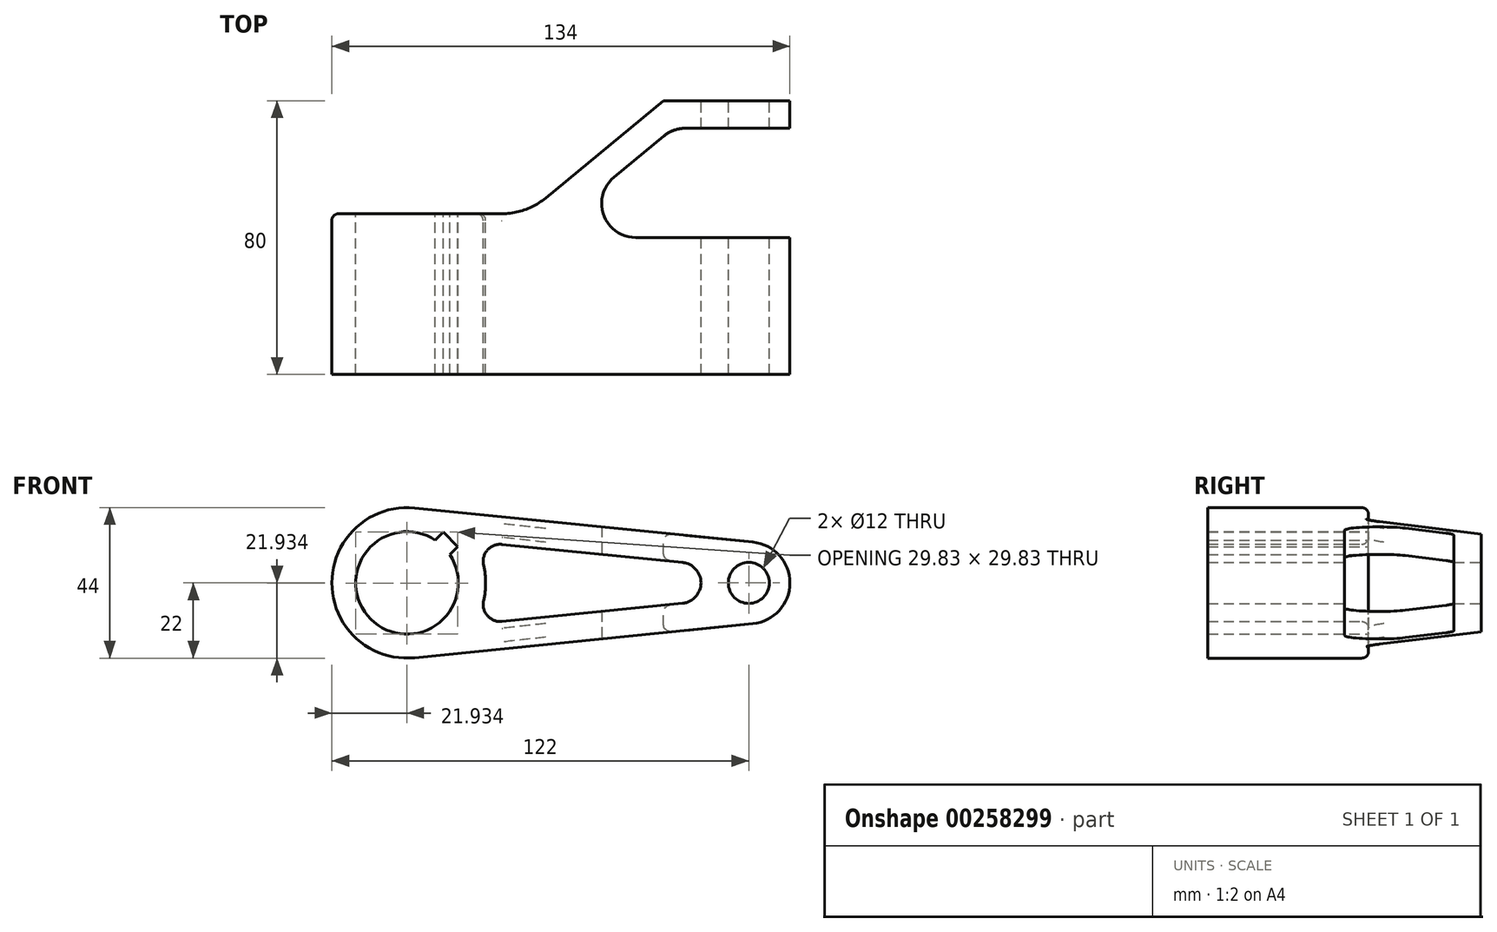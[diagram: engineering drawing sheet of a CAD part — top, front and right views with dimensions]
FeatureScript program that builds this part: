
annotation { "Feature Type Name" : "Feature", "Feature Type Description" : "" }
export const myFeature = defineFeature(function(context is Context, id is Id, definition is map)
    precondition{}
    {
        {
            var Q0;
            Q0=qCreatedBy(makeId("Front.planeOp"),FACE);
            var sketch = newSketch(context, id + "F0", { "sketchPlane" : qUnion([Q0])});
            skArc(sketch, "E0", {"start": v(2.2, 21.89) * mm, "mid": v(-22, 0) * mm, "end": v(2.2, -21.89) * mm});
            skLineSegment(sketch, "E1", {"start": v(2.2, 21.89) * mm, "end": v(101.2, 11.94) * mm});
            skLineSegment(sketch, "E2", {"start": v(2.2, -21.89) * mm, "end": v(101.2, -11.94) * mm});
            skArc(sketch, "E3", {"start": v(101.2, -11.94) * mm, "mid": v(112, 0) * mm, "end": v(101.2, 11.94) * mm});
            skArc(sketch, "E4", {"start": v(8.27, 12.51) * mm, "mid": v(-10.6, -10.6) * mm, "end": v(12.51, 8.27) * mm});
            skCircle(sketch, "E5", {"center": v(100, 0) * mm, "radius": 6 * mm});
            skLineSegment(sketch, "E6", {"start": v(0, 0) * mm, "end": v(100, 0) * mm, "construction": true});
            skArc(sketch, "E7", {"start": v(22.4, -5.18) * mm, "mid": v(23, 0) * mm, "end": v(22.4, 5.18) * mm});
            skLineSegment(sketch, "E8.0", {"start": v(27.78, 11.28) * mm, "end": v(80.6, 5.97) * mm});
            skLineSegment(sketch, "E9.0", {"start": v(27.78, -11.28) * mm, "end": v(80.6, -5.97) * mm});
            skArc(sketch, "E10", {"start": v(80.6, -5.97) * mm, "mid": v(86, 0) * mm, "end": v(80.6, 5.97) * mm});
            skPoint(sketch, "E11.visualSharp", {"position": v(19.56, 12.1) * mm});
            skArc(sketch, "E11.filletArc", {"start": v(27.78, 11.28) * mm, "mid": v(23.53, 9.6) * mm, "end": v(22.4, 5.18) * mm});
            skPoint(sketch, "E12.visualSharp", {"position": v(19.56, -12.1) * mm});
            skArc(sketch, "E12.filletArc", {"start": v(22.4, -5.18) * mm, "mid": v(23.53, -9.6) * mm, "end": v(27.78, -11.28) * mm});
            skLineSegment(sketch, "E13", {"start": v(8.27, 12.51) * mm, "end": v(10.6, 14.85) * mm});
            skLineSegment(sketch, "E14", {"start": v(10.6, 14.85) * mm, "end": v(14.85, 10.6) * mm});
            skLineSegment(sketch, "E15", {"start": v(14.85, 10.6) * mm, "end": v(12.51, 8.27) * mm});
            skLineSegment(sketch, "E16", {"start": v(0, 0) * mm, "end": v(12.73, 12.73) * mm, "construction": true});
            skArc(sketch, "E17", {"start": v(12.51, 8.27) * mm, "mid": v(10.6, 10.6) * mm, "end": v(8.27, 12.51) * mm});
            skSolve(sketch);
        }
        {
            var Q0;
            Q0 = qSketchRegion(id + "F0", true);
            extrude(context, id + "F1", {"entities" : qUnion([Q0]), "endBound" : BoundingType.SYMMETRIC, "offsetDistance" : 25 * mm, "depth" : 80 * mm});
        }
        {
            var Q0;
            Q0=qCreatedBy(makeId("Top.planeOp"),FACE);
            var sketch = newSketch(context, id + "F2", { "sketchPlane" : qUnion([Q0])});
            skLineSegment(sketch, "E18", {"start": v(-22, 7) * mm, "end": v(-22, 40) * mm});
            skLineSegment(sketch, "E19", {"start": v(112, 32) * mm, "end": v(112, 0) * mm});
            skLineSegment(sketch, "E20", {"start": v(-22, 40) * mm, "end": v(75, 40) * mm});
            skLineSegment(sketch, "E21", {"start": v(75, 40) * mm, "end": v(35, 7) * mm});
            skLineSegment(sketch, "E22", {"start": v(35, 7) * mm, "end": v(-22, 7) * mm});
            skLineSegment(sketch, "E23", {"start": v(-22, 0) * mm, "end": v(112, 0) * mm, "construction": true});
            skLineSegment(sketch, "E24", {"start": v(0, 40) * mm, "end": v(0, -40) * mm, "construction": true});
            skLineSegment(sketch, "E25", {"start": v(112, 32) * mm, "end": v(77.87, 32) * mm});
            skLineSegment(sketch, "E26", {"start": v(77.87, 32) * mm, "end": v(39.09, 0) * mm});
            skLineSegment(sketch, "E27", {"start": v(39.09, 0) * mm, "end": v(112, 0) * mm});
            skPoint(sketch, "E28.orphan", {"position": v(112, 40) * mm});
            skPoint(sketch, "E29.orphan", {"position": v(112, -40) * mm});
            skPoint(sketch, "E30.orphan", {"position": v(-22, -40) * mm});
            skSolve(sketch);
        }
        {
            var Q0;
            Q0 = qSketchRegion(id + "F2", true);
            extrude(context, id + "F3", {"entities" : qUnion([Q0]), "operationType" : NewBodyOperationType.REMOVE, "endBound" : BoundingType.THROUGH_ALL, "oppositeDirection" : true, "depth" : 25 * mm, "hasSecondDirection" : true, "secondDirectionBound" : SecondDirectionBoundingType.THROUGH_ALL, "secondDirectionOppositeDirection" : false, "secondDirectionDepth" : 25 * mm});
        }
        {
            var Q0;
            {var subQ0=sQuery(id+"F2.wireOp",EDGE,"E27");var subQ1=sQuery(id+"F2.wireOp",EDGE,"E26");Q0=makeQuery(id+"Fcrfvm8RNoEdja2_1.1.F3.boolean.opBoolean","MERGE",EDGE,{"derivedFrom":[makeQuery(id+"F3.boolean.opBoolean","COPY",EDGE,{"disambiguationData":[TD([makeQuery(id+"F1.opExtrude","SWEPT_FACE",FACE,{"disambiguationData":[OSD([sQuery(id+"F0.wireOp",EDGE,"E1")])]})])],"derivedFrom":makeQuery(id+"F3.opExtrude","SWEPT_EDGE",EDGE,{"disambiguationData":[OSD([subQ1,subQ0])]})}),makeQuery(id+"Fcrfvm8RNoEdja2_1.1.F3.opExtrude","SWEPT_EDGE",EDGE,{"disambiguationData":[OSD([subQ1,subQ0])]})]});}
            var Q1;
            {var subQ0=sQuery(id+"F2.wireOp",EDGE,"E27");var subQ1=sQuery(id+"F2.wireOp",EDGE,"E26");Q1=makeQuery(id+"Fcrfvm8RNoEdja2_1.1.F3.boolean.opBoolean","MERGE",EDGE,{"derivedFrom":[makeQuery(id+"F3.boolean.opBoolean","COPY",EDGE,{"disambiguationData":[TD([makeQuery(id+"F1.opExtrude","SWEPT_FACE",FACE,{"disambiguationData":[OSD([sQuery(id+"F0.wireOp",EDGE,"E2")])]})])],"derivedFrom":makeQuery(id+"F3.opExtrude","SWEPT_EDGE",EDGE,{"disambiguationData":[OSD([subQ1,subQ0])]})}),makeQuery(id+"Fcrfvm8RNoEdja2_1.1.F3.opExtrude","SWEPT_EDGE",EDGE,{"disambiguationData":[OSD([subQ1,subQ0])]})]});}
            var Q2;
            {var subQ0=sQuery(id+"F2.wireOp",EDGE,"E25");var subQ1=sQuery(id+"F2.wireOp",EDGE,"E26");Q2=makeQuery(id+"F3.boolean.opBoolean","COPY",EDGE,{"disambiguationData":[TD([makeQuery(id+"F1.opExtrude","SWEPT_FACE",FACE,{"disambiguationData":[OSD([sQuery(id+"F0.wireOp",EDGE,"E1")])]})])],"derivedFrom":makeQuery(id+"F3.opExtrude","SWEPT_EDGE",EDGE,{"disambiguationData":[OSD([subQ0,subQ1])]})});}
            var Q3;
            {var subQ0=sQuery(id+"F2.wireOp",EDGE,"E25");var subQ1=sQuery(id+"F2.wireOp",EDGE,"E26");Q3=makeQuery(id+"F3.boolean.opBoolean","COPY",EDGE,{"disambiguationData":[TD([makeQuery(id+"F1.opExtrude","SWEPT_FACE",FACE,{"disambiguationData":[OSD([sQuery(id+"F0.wireOp",EDGE,"E2")])]})])],"derivedFrom":makeQuery(id+"F3.opExtrude","SWEPT_EDGE",EDGE,{"disambiguationData":[OSD([subQ0,subQ1])]})});}
            var Q4;
            {var subQ0=sQuery(id+"F2.wireOp",EDGE,"E25");var subQ1=sQuery(id+"F2.wireOp",EDGE,"E26");Q4=makeQuery(id+"Fcrfvm8RNoEdja2_1.1.F3.boolean.opBoolean","COPY",EDGE,{"disambiguationData":[TD([makeQuery(id+"F1.opExtrude","SWEPT_FACE",FACE,{"disambiguationData":[OSD([sQuery(id+"F0.wireOp",EDGE,"E2")])]})])],"derivedFrom":makeQuery(id+"Fcrfvm8RNoEdja2_1.1.F3.opExtrude","SWEPT_EDGE",EDGE,{"disambiguationData":[OSD([subQ0,subQ1])]})});}
            var Q5;
            {var subQ0=sQuery(id+"F2.wireOp",EDGE,"E26");var subQ1=sQuery(id+"F2.wireOp",EDGE,"E25");Q5=makeQuery(id+"Fcrfvm8RNoEdja2_1.1.F3.boolean.opBoolean","COPY",EDGE,{"disambiguationData":[TD([makeQuery(id+"F1.opExtrude","SWEPT_FACE",FACE,{"disambiguationData":[OSD([sQuery(id+"F0.wireOp",EDGE,"E1")])]})])],"derivedFrom":makeQuery(id+"Fcrfvm8RNoEdja2_1.1.F3.opExtrude","SWEPT_EDGE",EDGE,{"disambiguationData":[OSD([subQ1,subQ0])]})});}
            fillet(context, id + "F4", {"entities" : qUnion([Q0, Q1, Q2, Q3, Q4, Q5]), "radius" : 10 * mm, "tangentPropagation" : true, "allowEdgeOverflow" : false});
        }
        {
            var Q0;
            {var subQ1=sQuery(id+"F0.wireOp",EDGE,"E1");var subQ2=sQuery(id+"F2.wireOp",EDGE,"E21");Q0=makeQuery(id+"F3.boolean.opBoolean","COPY",EDGE,{"disambiguationData":[TD([makeQuery(id+"F1.opExtrude","SWEPT_FACE",FACE,{"disambiguationData":[OSD([subQ1])]})])],"derivedFrom":makeQuery(id+"F3.opExtrude","SWEPT_EDGE",EDGE,{"disambiguationData":[OSD([sQuery(id+"F2.wireOp",EDGE,"E20"),subQ2])]})});}
            var Q1;
            {var subQ1=sQuery(id+"F0.wireOp",EDGE,"E2");var subQ2=sQuery(id+"F2.wireOp",EDGE,"E21");Q1=makeQuery(id+"F3.boolean.opBoolean","COPY",EDGE,{"disambiguationData":[TD([makeQuery(id+"F1.opExtrude","SWEPT_FACE",FACE,{"disambiguationData":[OSD([subQ1])]})])],"derivedFrom":makeQuery(id+"F3.opExtrude","SWEPT_EDGE",EDGE,{"disambiguationData":[OSD([sQuery(id+"F2.wireOp",EDGE,"E20"),subQ2])]})});}
            var Q2;
            {var subQ0=sQuery(id+"F2.wireOp",EDGE,"E21");var subQ1=sQuery(id+"F2.wireOp",EDGE,"E22");Q2=makeQuery(id+"F3.boolean.opBoolean","COPY",EDGE,{"disambiguationData":[TD([makeQuery(id+"F1.opExtrude","SWEPT_FACE",FACE,{"disambiguationData":[OSD([sQuery(id+"F0.wireOp",EDGE,"E2")])]})])],"derivedFrom":makeQuery(id+"F3.opExtrude","SWEPT_EDGE",EDGE,{"disambiguationData":[OSD([subQ0,subQ1])]})});}
            var Q3;
            {var subQ0=sQuery(id+"F2.wireOp",EDGE,"E21");var subQ1=sQuery(id+"F2.wireOp",EDGE,"E22");Q3=makeQuery(id+"F3.boolean.opBoolean","COPY",EDGE,{"disambiguationData":[TD([makeQuery(id+"F1.opExtrude","SWEPT_FACE",FACE,{"disambiguationData":[OSD([sQuery(id+"F0.wireOp",EDGE,"E1")])]})])],"derivedFrom":makeQuery(id+"F3.opExtrude","SWEPT_EDGE",EDGE,{"disambiguationData":[OSD([subQ0,subQ1])]})});}
            var Q4;
            {var subQ0=sQuery(id+"F2.wireOp",EDGE,"E21");var subQ1=sQuery(id+"F2.wireOp",EDGE,"E22");Q4=makeQuery(id+"Fcrfvm8RNoEdja2_1.1.F3.boolean.opBoolean","COPY",EDGE,{"disambiguationData":[TD([makeQuery(id+"F1.opExtrude","SWEPT_FACE",FACE,{"disambiguationData":[OSD([sQuery(id+"F0.wireOp",EDGE,"E1")])]})])],"derivedFrom":makeQuery(id+"Fcrfvm8RNoEdja2_1.1.F3.opExtrude","SWEPT_EDGE",EDGE,{"disambiguationData":[OSD([subQ0,subQ1])]})});}
            var Q5;
            {var subQ0=sQuery(id+"F2.wireOp",EDGE,"E21");var subQ1=sQuery(id+"F2.wireOp",EDGE,"E22");Q5=makeQuery(id+"Fcrfvm8RNoEdja2_1.1.F3.boolean.opBoolean","COPY",EDGE,{"disambiguationData":[TD([makeQuery(id+"F1.opExtrude","SWEPT_FACE",FACE,{"disambiguationData":[OSD([sQuery(id+"F0.wireOp",EDGE,"E2")])]})])],"derivedFrom":makeQuery(id+"Fcrfvm8RNoEdja2_1.1.F3.opExtrude","SWEPT_EDGE",EDGE,{"disambiguationData":[OSD([subQ0,subQ1])]})});}
            var Q6;
            {var subQ1=sQuery(id+"F0.wireOp",EDGE,"E2");var subQ2=sQuery(id+"F2.wireOp",EDGE,"E21");Q6=makeQuery(id+"Fcrfvm8RNoEdja2_1.1.F3.boolean.opBoolean","COPY",EDGE,{"disambiguationData":[TD([makeQuery(id+"F1.opExtrude","SWEPT_FACE",FACE,{"disambiguationData":[OSD([subQ1])]})])],"derivedFrom":makeQuery(id+"Fcrfvm8RNoEdja2_1.1.F3.opExtrude","SWEPT_EDGE",EDGE,{"disambiguationData":[OSD([sQuery(id+"F2.wireOp",EDGE,"E20"),subQ2])]})});}
            var Q7;
            {var subQ1=sQuery(id+"F0.wireOp",EDGE,"E1");var subQ2=sQuery(id+"F2.wireOp",EDGE,"E21");Q7=makeQuery(id+"Fcrfvm8RNoEdja2_1.1.F3.boolean.opBoolean","COPY",EDGE,{"disambiguationData":[TD([makeQuery(id+"F1.opExtrude","SWEPT_FACE",FACE,{"disambiguationData":[OSD([subQ1])]})])],"derivedFrom":makeQuery(id+"Fcrfvm8RNoEdja2_1.1.F3.opExtrude","SWEPT_EDGE",EDGE,{"disambiguationData":[OSD([sQuery(id+"F2.wireOp",EDGE,"E20"),subQ2])]})});}
            fillet(context, id + "F5", {"entities" : qUnion([Q0, Q1, Q2, Q3, Q4, Q5, Q6, Q7]), "radius" : 20 * mm, "tangentPropagation" : true, "allowEdgeOverflow" : false});
        }
        {
            var Q0;
            Q0=makeQuery(id+"Fcrfvm8RNoEdja2_1.1.F3.boolean.opBoolean","INTERSECT",EDGE,{"derivedFrom":[makeQuery(id+"F1.opExtrude","SWEPT_FACE",FACE,{"disambiguationData":[OSD([sQuery(id+"F0.wireOp",EDGE,"E0")])]}),makeQuery(id+"Fcrfvm8RNoEdja2_1.1.F3.opExtrude","SWEPT_FACE",FACE,{"disambiguationData":[OSD([sQuery(id+"F2.wireOp",EDGE,"E22")])]})]});
            var Q1;
            Q1=makeQuery(id+"F3.boolean.opBoolean","INTERSECT",EDGE,{"derivedFrom":[makeQuery(id+"F1.opExtrude","SWEPT_FACE",FACE,{"disambiguationData":[OSD([sQuery(id+"F0.wireOp",EDGE,"E0")])]}),makeQuery(id+"F3.opExtrude","SWEPT_FACE",FACE,{"disambiguationData":[OSD([sQuery(id+"F2.wireOp",EDGE,"E22")])]})]});
            var Q2;
            {var subQ0=makeQuery(id+"F1.opExtrude","SWEPT_FACE",FACE,{"disambiguationData":[OSD([sQuery(id+"F0.wireOp",EDGE,"E8.0")])]});var subQ1=sQuery(id+"F2.wireOp",EDGE,"E22");var subQ2=sQuery(id+"F2.wireOp",EDGE,"E21");Q2=makeQuery(id+"F5.opFillet","BLEND_EDGE",EDGE,{"blendedFrom":[makeQuery(id+"Fcrfvm8RNoEdja2_1.1.F3.boolean.opBoolean","COPY",EDGE,{"disambiguationData":[TD([makeQuery(id+"F1.opExtrude","SWEPT_FACE",FACE,{"disambiguationData":[OSD([sQuery(id+"F0.wireOp",EDGE,"E1")])]})])],"derivedFrom":makeQuery(id+"Fcrfvm8RNoEdja2_1.1.F3.opExtrude","SWEPT_EDGE",EDGE,{"disambiguationData":[OSD([subQ2,subQ1])]})}),subQ0],"blendedInto":[subQ0]});}
            var Q3;
            {var subQ0=makeQuery(id+"F1.opExtrude","SWEPT_FACE",FACE,{"disambiguationData":[OSD([sQuery(id+"F0.wireOp",EDGE,"E8.0")])]});var subQ1=sQuery(id+"F2.wireOp",EDGE,"E21");var subQ2=sQuery(id+"F2.wireOp",EDGE,"E22");Q3=makeQuery(id+"F5.opFillet","BLEND_EDGE",EDGE,{"blendedFrom":[makeQuery(id+"F3.boolean.opBoolean","COPY",EDGE,{"disambiguationData":[TD([makeQuery(id+"F1.opExtrude","SWEPT_FACE",FACE,{"disambiguationData":[OSD([sQuery(id+"F0.wireOp",EDGE,"E1")])]})])],"derivedFrom":makeQuery(id+"F3.opExtrude","SWEPT_EDGE",EDGE,{"disambiguationData":[OSD([subQ1,subQ2])]})}),subQ0],"blendedInto":[subQ0]});}
            fillet(context, id + "F6", {"entities" : qUnion([Q0, Q1, Q2, Q3]), "radius" : 2 * mm, "tangentPropagation" : true, "allowEdgeOverflow" : false});
        }
    });
